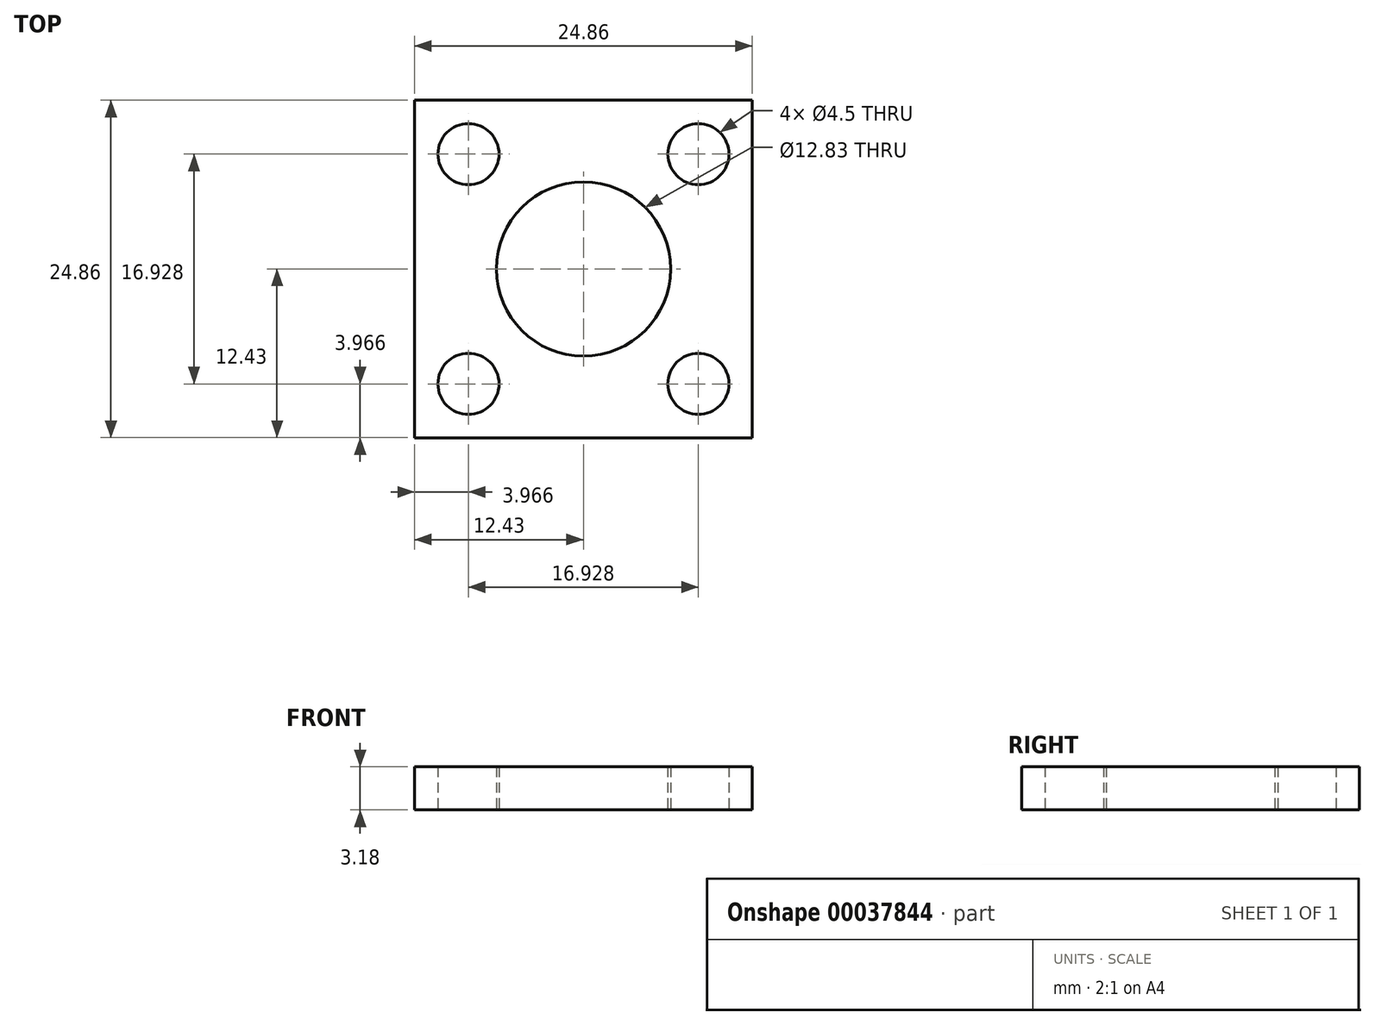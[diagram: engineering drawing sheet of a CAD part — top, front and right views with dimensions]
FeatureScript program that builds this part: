
annotation { "Feature Type Name" : "Feature", "Feature Type Description" : "" }
export const myFeature = defineFeature(function(context is Context, id is Id, definition is map)
    precondition{}
    {
        {
            var Q0;
            Q0=qCreatedBy(makeId("Top.planeOp"),FACE);
            var sketch = newSketch(context, id + "F0", { "sketchPlane" : qUnion([Q0])});
            skLineSegment(sketch, "E0.rect.bottom", {"start": v(12.43, 12.43) * mm, "end": v(-12.43, 12.43) * mm});
            skLineSegment(sketch, "E0.rect.top", {"start": v(12.43, -12.43) * mm, "end": v(-12.43, -12.43) * mm});
            skLineSegment(sketch, "E0.rect.left", {"start": v(12.43, 12.43) * mm, "end": v(12.43, -12.43) * mm});
            skLineSegment(sketch, "E0.rect.right", {"start": v(-12.43, 12.43) * mm, "end": v(-12.43, -12.43) * mm});
            skPoint(sketch, "E0.rect.middle", {"position": v(0, 0) * mm});
            skLineSegment(sketch, "E1.rect.bottom", {"start": v(8.46, 8.46) * mm, "end": v(-8.46, 8.46) * mm, "construction": true});
            skLineSegment(sketch, "E1.rect.top", {"start": v(8.46, -8.46) * mm, "end": v(-8.46, -8.46) * mm, "construction": true});
            skLineSegment(sketch, "E1.rect.left", {"start": v(8.46, 8.46) * mm, "end": v(8.46, -8.46) * mm, "construction": true});
            skLineSegment(sketch, "E1.rect.right", {"start": v(-8.46, 8.46) * mm, "end": v(-8.46, -8.46) * mm, "construction": true});
            skCircle(sketch, "E2", {"center": v(8.46, 8.46) * mm, "radius": 3.97 * mm, "construction": true});
            skCircle(sketch, "E3", {"center": v(-8.46, 8.46) * mm, "radius": 2.25 * mm});
            skCircle(sketch, "E4", {"center": v(8.46, 8.46) * mm, "radius": 2.25 * mm});
            skCircle(sketch, "E5", {"center": v(-8.46, -8.46) * mm, "radius": 2.25 * mm});
            skCircle(sketch, "E6", {"center": v(8.46, -8.46) * mm, "radius": 2.25 * mm});
            skCircle(sketch, "E7", {"center": v(0, 0) * mm, "radius": 6.41 * mm});
            skSolve(sketch);
        }
        {
            var Q0;
            Q0 = qSketchRegion(id + "F0", true);
            extrude(context, id + "F1", {"entities" : qUnion([Q0]), "depth" : 3.17 * mm});
        }
    });
